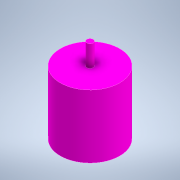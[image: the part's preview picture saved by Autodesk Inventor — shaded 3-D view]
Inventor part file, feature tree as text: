
AUTODESK INVENTOR PART (.ipt)
format: ipt  version: 2021 (Build 250183000, 183)  size: 99,328 bytes
history: native  units: mm
features: revolve x1, sketch x1
ambient origin geometry x8: Origin, YZ Plane, XZ Plane, XY Plane, X Axis, Y Axis, Z Axis, Center Point
bodies: Solid1 (feature_tree)
feature tree (2):
  revolve  "Revolution1"  [1 undecoded]
  sketch  "Sketch1"  dims[d0=1.5mm d1=39.7mm d2=13.95mm d3=10.0mm d4=90.0deg]
note: 1 required parameter value undecoded (feature->parameter linkage not recoverable at this tier; creation-order binding heuristic only, values carry confidence <= 0.55)
